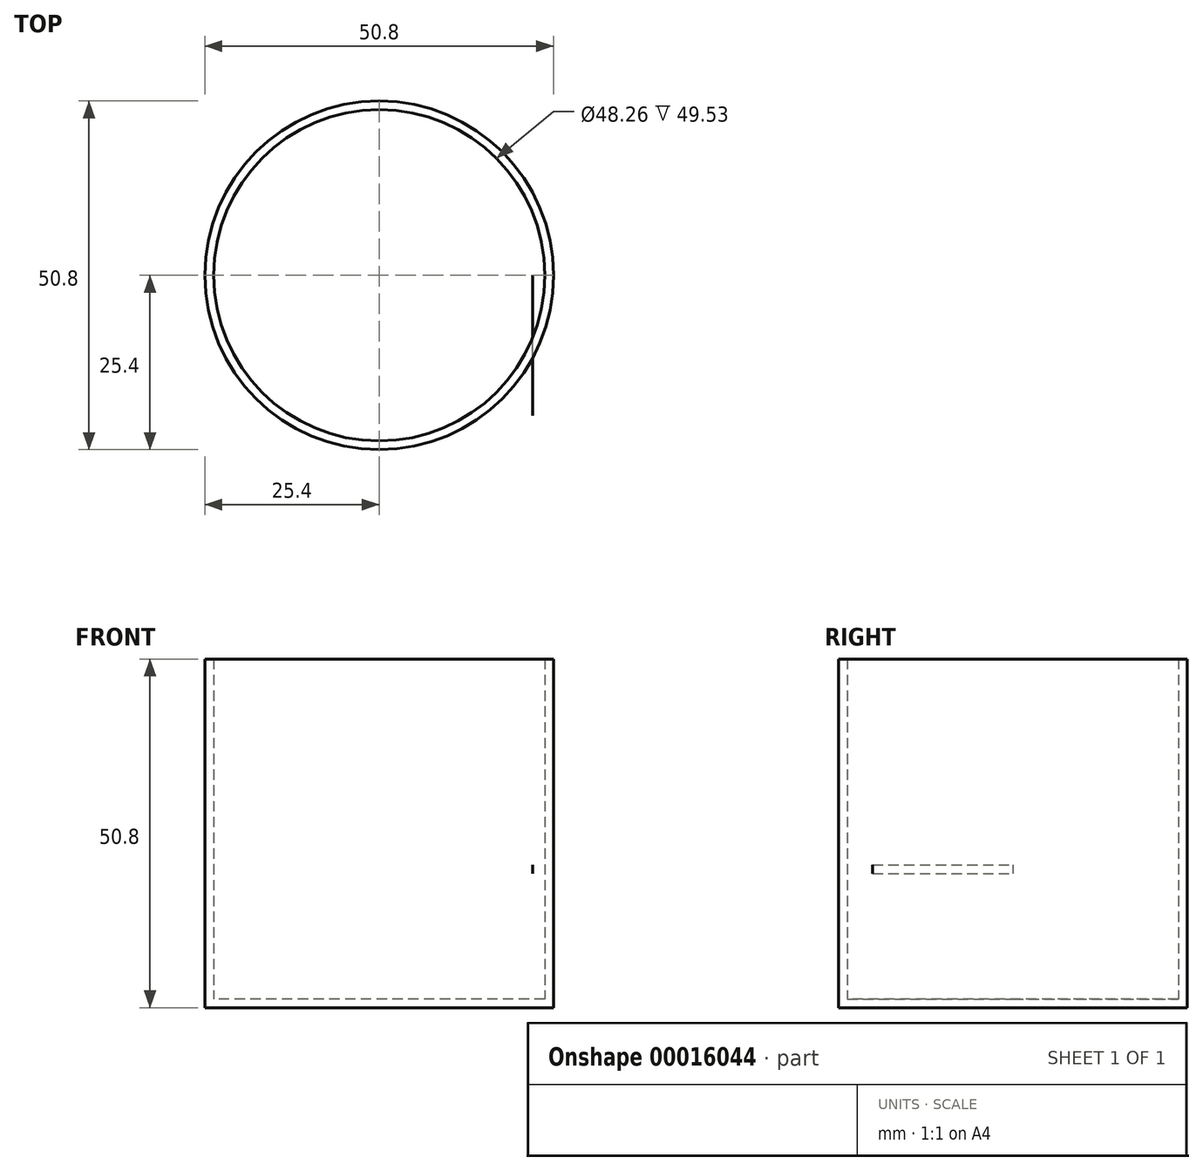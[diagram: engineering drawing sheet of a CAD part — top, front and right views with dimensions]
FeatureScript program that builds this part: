
annotation { "Feature Type Name" : "Feature", "Feature Type Description" : "" }
export const myFeature = defineFeature(function(context is Context, id is Id, definition is map)
    precondition{}
    {
        {
            var Q0;
            Q0=qCreatedBy(makeId("Top.planeOp"),FACE);
            var sketch = newSketch(context, id + "F0", { "sketchPlane" : qUnion([Q0])});
            skCircle(sketch, "E0", {"center": v(0, 0) * mm, "radius": 25.4 * mm});
            skSolve(sketch);
        }
        {
            var Q0;
            Q0=makeQuery(id+"F0.imprint","IMPRINT",FACE,{"disambiguationData":[TD([[makeQuery(id+"F0.imprint","IMPRINT",EDGE,{"derivedFrom":sQuery(id+"F0.wireOp",EDGE,"E0")}),1.0]])]});
            extrude(context, id + "F1", {"entities" : qUnion([Q0]), "depth" : 50.8 * mm});
        }
        {
            var Q0;
            Q0=makeQuery(id+"F1.opExtrude","CAP_FACE",FACE,{"disambiguationData":[OSD([sQuery(id+"F0.wireOp",EDGE,"E0")])],"isStart":false});
            shell(context, id + "F2", {"entities" : qUnion([Q0]), "thickness" : 1.27 * mm});
        }
        {
            var Q0;
            Q0=qCreatedBy(makeId("Front.planeOp"),FACE);
            var sketch = newSketch(context, id + "F3", { "sketchPlane" : qUnion([Q0])});
            skLineSegment(sketch, "E1.rect.bottom", {"start": v(22.35, 27.88) * mm, "end": v(-22.35, 27.88) * mm});
            skLineSegment(sketch, "E1.rect.top", {"start": v(22.35, 19.33) * mm, "end": v(-22.35, 19.33) * mm});
            skLineSegment(sketch, "E1.rect.left", {"start": v(22.35, 27.88) * mm, "end": v(22.35, 19.33) * mm});
            skLineSegment(sketch, "E1.rect.right", {"start": v(-22.35, 27.88) * mm, "end": v(-22.35, 19.33) * mm});
            skPoint(sketch, "E1.rect.middle", {"position": v(0, 23.6) * mm});
            skText(sketch, "E2", { "text": "Da Best", "fontName": "OpenSans-Bold.ttf"});
            const initialGuessF3  = {"E2": [-0.02235, 0.01933, 1, 0, 0.00855]};
            skSetInitialGuess(sketch, initialGuessF3);
            skSolve(sketch);
        }
        {
            var Q0;
            Q0=makeQuery(id+"F3.imprint","IMPRINT",FACE,{"disambiguationData":[TD([[makeQuery(id+"F3.imprint","IMPRINT",EDGE,{"derivedFrom":sQuery(id+"F3.wireOp",EDGE,"E2.sketch_text.stroke-108")}),-1.0]])]});
            extrude(context, id + "F4", {"entities" : qUnion([Q0]), "depth" : 20.44 * mm});
        }
    });
